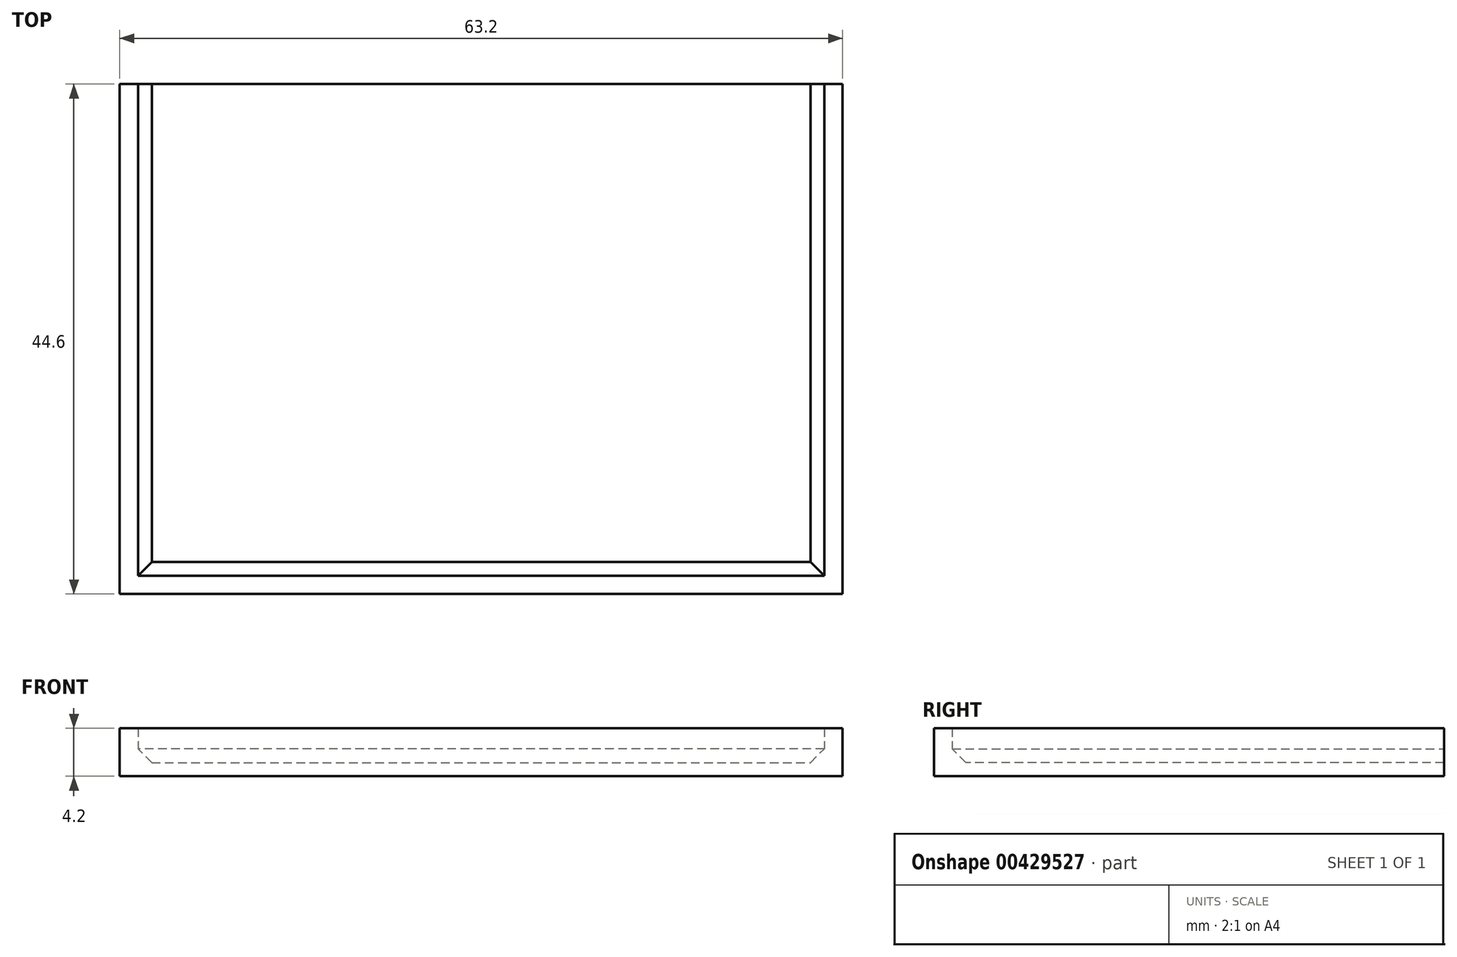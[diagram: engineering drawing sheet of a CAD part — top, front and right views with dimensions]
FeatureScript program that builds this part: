
annotation { "Feature Type Name" : "Feature", "Feature Type Description" : "" }
export const myFeature = defineFeature(function(context is Context, id is Id, definition is map)
    precondition{}
    {
        {
            var Q0;
            Q0=qCreatedBy(makeId("Top.planeOp"),FACE);
            var sketch = newSketch(context, id + "F0", { "sketchPlane" : qUnion([Q0])});
            skLineSegment(sketch, "E0.bottom", {"start": v(-30.29, 27.4) * mm, "end": v(32.91, 27.4) * mm});
            skLineSegment(sketch, "E0.top", {"start": v(-28.69, -15.6) * mm, "end": v(31.31, -15.6) * mm});
            skLineSegment(sketch, "E0.left", {"start": v(-28.69, 27.4) * mm, "end": v(-28.69, -15.6) * mm});
            skLineSegment(sketch, "E0.right", {"start": v(31.31, 27.4) * mm, "end": v(31.31, -15.6) * mm});
            skLineSegment(sketch, "E1.2", {"start": v(32.91, 27.4) * mm, "end": v(32.91, -17.2) * mm});
            skLineSegment(sketch, "E1.3", {"start": v(-30.29, -17.2) * mm, "end": v(32.91, -17.2) * mm});
            skLineSegment(sketch, "E2", {"start": v(-30.29, 27.4) * mm, "end": v(-30.29, -17.2) * mm});
            skSolve(sketch);
        }
        {
            var Q0;
            Q0=makeQuery(id+"F0.imprint","IMPRINT",FACE,{"disambiguationData":[TD([[makeQuery(id+"F0.imprint","IMPRINT",EDGE,{"derivedFrom":sQuery(id+"F0.wireOp",EDGE,"E0.bottom")}),-1.0]])]});
            extrude(context, id + "F1", {"entities" : qUnion([Q0]), "depth" : 4.2 * mm});
        }
        {
            var Q0;
            Q0=makeQuery(id+"F0.imprint","IMPRINT",FACE,{"disambiguationData":[TD([[makeQuery(id+"F0.imprint","IMPRINT",EDGE,{"derivedFrom":sQuery(id+"F0.wireOp",EDGE,"E0.top")}),-1.0]])]});
            var Q1;
            Q1=makeQuery(id+"F0.imprint","IMPRINT",FACE,{"disambiguationData":[TD([[makeQuery(id+"F0.imprint","IMPRINT",EDGE,{"derivedFrom":sQuery(id+"F0.wireOp",EDGE,"E0.top")}),1.0]])]});
            extrude(context, id + "F2", {"entities" : qUnion([Q0, Q1]), "operationType" : NewBodyOperationType.ADD, "depth" : 1.2 * mm});
        }
        {
            var Q0;
            Q0=makeQuery(id+"F2.boolean.opBoolean","INTERSECT",EDGE,{"derivedFrom":[makeQuery(id+"F1.opExtrude","SWEPT_FACE",FACE,{"disambiguationData":[OSD([sQuery(id+"F0.wireOp",EDGE,"E0.left")])]}),makeQuery(id+"F2.opExtrude","CAP_FACE",FACE,{"disambiguationData":[OSD([sQuery(id+"F0.wireOp",EDGE,"E0.bottom"),sQuery(id+"F0.wireOp",EDGE,"E1.2"),sQuery(id+"F0.wireOp",EDGE,"E1.3"),sQuery(id+"F0.wireOp",EDGE,"E2")])],"isStart":false})]});
            var Q1;
            Q1=makeQuery(id+"F2.boolean.opBoolean","INTERSECT",EDGE,{"derivedFrom":[makeQuery(id+"F1.opExtrude","SWEPT_FACE",FACE,{"disambiguationData":[OSD([sQuery(id+"F0.wireOp",EDGE,"E0.top")])]}),makeQuery(id+"F2.opExtrude","CAP_FACE",FACE,{"disambiguationData":[OSD([sQuery(id+"F0.wireOp",EDGE,"E0.bottom"),sQuery(id+"F0.wireOp",EDGE,"E1.2"),sQuery(id+"F0.wireOp",EDGE,"E1.3"),sQuery(id+"F0.wireOp",EDGE,"E2")])],"isStart":false})]});
            var Q2;
            Q2=makeQuery(id+"F2.boolean.opBoolean","INTERSECT",EDGE,{"derivedFrom":[makeQuery(id+"F1.opExtrude","SWEPT_FACE",FACE,{"disambiguationData":[OSD([sQuery(id+"F0.wireOp",EDGE,"E0.right")])]}),makeQuery(id+"F2.opExtrude","CAP_FACE",FACE,{"disambiguationData":[OSD([sQuery(id+"F0.wireOp",EDGE,"E0.bottom"),sQuery(id+"F0.wireOp",EDGE,"E1.2"),sQuery(id+"F0.wireOp",EDGE,"E1.3"),sQuery(id+"F0.wireOp",EDGE,"E2")])],"isStart":false})]});
            chamfer(context, id + "F3", {"entities" : qUnion([Q0, Q1, Q2]), "width" : 1.2 * mm, "tangentPropagation" : true});
        }
    });
